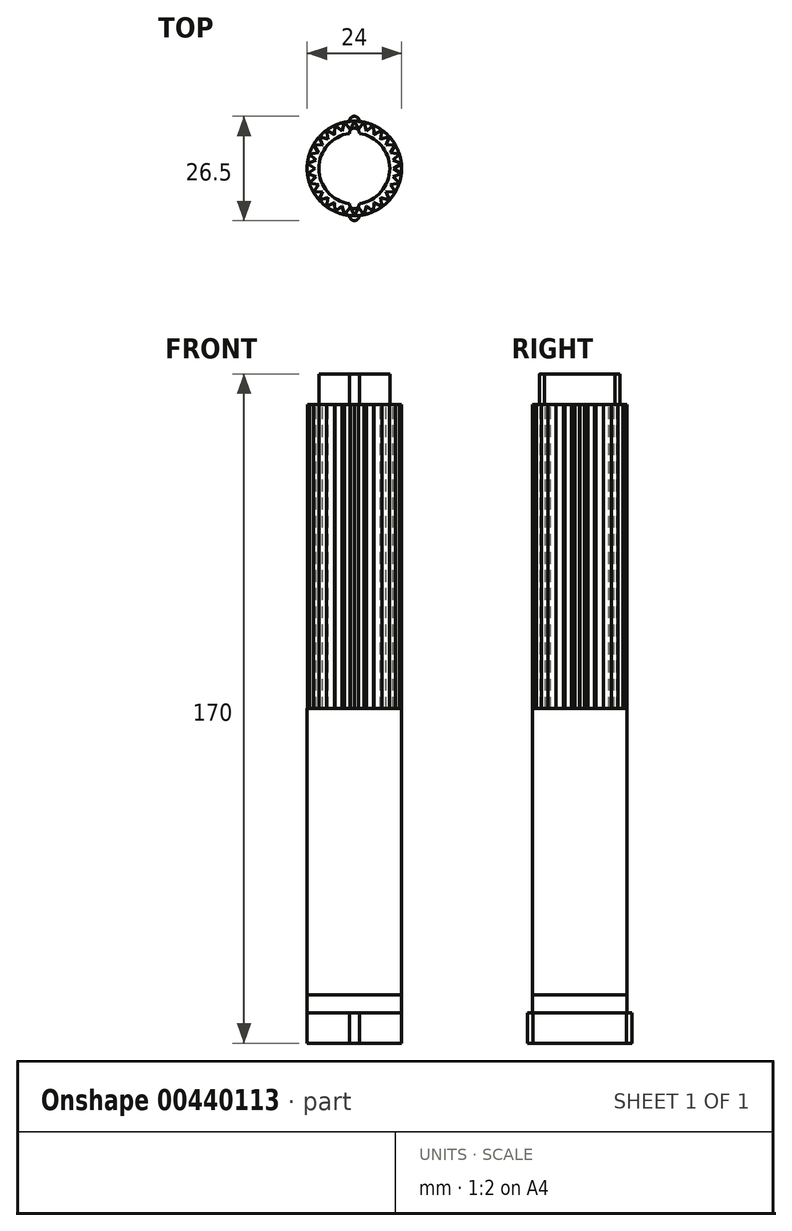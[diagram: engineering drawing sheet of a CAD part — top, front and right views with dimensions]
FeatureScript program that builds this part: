
annotation { "Feature Type Name" : "Feature", "Feature Type Description" : "" }
export const myFeature = defineFeature(function(context is Context, id is Id, definition is map)
    precondition{}
    {
        {
            var Q0;
            Q0=qCreatedBy(makeId("Top.planeOp"),FACE);
            var sketch = newSketch(context, id + "F0", { "sketchPlane" : qUnion([Q0])});
            skCircle(sketch, "E0", {"center": v(0, 0) * mm, "radius": 12 * mm});
            skSolve(sketch);
        }
        {
            var Q0;
            Q0 = qSketchRegion(id + "F0", true);
            extrude(context, id + "F1", {"entities" : qUnion([Q0]), "depth" : 72.75 * mm});
        }
        {
            var Q0;
            Q0=qCreatedBy(makeId("Top.planeOp"),FACE);
            cPlane(context, id + "F2", {"entities" : qUnion([Q0]), "cplaneType" : CPlaneType.OFFSET, "offset" : 75 * mm, "width" : 150 * mm, "height" : 150 * mm});
        }
        {
            var Q0;
            Q0=qCreatedBy(makeId("Top.planeOp"),FACE);
            cPlane(context, id + "F3", {"entities" : qUnion([Q0]), "cplaneType" : CPlaneType.OFFSET, "offset" : 150 * mm, "width" : 150 * mm, "height" : 150 * mm});
        }
        {
            var Q0;
            Q0=qCreatedBy(id+"F3.planeOp",FACE);
            var sketch = newSketch(context, id + "F4", { "sketchPlane" : qUnion([Q0])});
            skCircle(sketch, "E1", {"center": v(0, 0) * mm, "radius": 9 * mm});
            skCircle(sketch, "E2", {"center": v(0, 9) * mm, "radius": 1.25 * mm});
            skCircle(sketch, "E3", {"center": v(0, -9) * mm, "radius": 1.25 * mm});
            skSolve(sketch);
        }
        {
            var Q0;
            Q0 = qSketchRegion(id + "F4", true);
            extrude(context, id + "F5", {"entities" : qUnion([Q0]), "operationType" : NewBodyOperationType.ADD, "depth" : 7.75 * mm});
        }
        {
            var Q0;
            Q0=qCreatedBy(id+"F3.planeOp",FACE);
            var sketch = newSketch(context, id + "F6", { "sketchPlane" : qUnion([Q0])});
            skCircle(sketch, "E4", {"center": v(0, 0) * mm, "radius": 10 * mm});
            skLineSegment(sketch, "E5", {"start": v(0, 12) * mm, "end": v(-1.04, 9.95) * mm});
            skLineSegment(sketch, "E6", {"start": v(0, 12) * mm, "end": v(1.04, 9.95) * mm});
            skLineSegment(sketch, "E7.1.0", {"start": v(-2.5, 11.74) * mm, "end": v(-3.08, 9.51) * mm});
            skLineSegment(sketch, "E7.1.1", {"start": v(-2.5, 11.74) * mm, "end": v(-1.06, 9.94) * mm});
            skLineSegment(sketch, "E7.2.0", {"start": v(-4.88, 10.96) * mm, "end": v(-5, 8.67) * mm});
            skLineSegment(sketch, "E7.2.1", {"start": v(-4.88, 10.96) * mm, "end": v(-3.1, 9.5) * mm});
            skLineSegment(sketch, "E7.3.0", {"start": v(-7.05, 9.7) * mm, "end": v(-6.68, 7.44) * mm});
            skLineSegment(sketch, "E7.3.1", {"start": v(-7.05, 9.7) * mm, "end": v(-5, 8.66) * mm});
            skLineSegment(sketch, "E7.4.0", {"start": v(-8.92, 8.03) * mm, "end": v(-8.08, 5.89) * mm});
            skLineSegment(sketch, "E7.4.1", {"start": v(-8.92, 8.03) * mm, "end": v(-6.7, 7.42) * mm});
            skLineSegment(sketch, "E7.5.0", {"start": v(-10.4, 6) * mm, "end": v(-9.13, 4.08) * mm});
            skLineSegment(sketch, "E7.5.1", {"start": v(-10.4, 6) * mm, "end": v(-8.1, 5.87) * mm});
            skLineSegment(sketch, "E7.6.0", {"start": v(-11.41, 3.7) * mm, "end": v(-9.78, 2.09) * mm});
            skLineSegment(sketch, "E7.6.1", {"start": v(-11.41, 3.7) * mm, "end": v(-9.14, 4.06) * mm});
            skLineSegment(sketch, "E7.7.0", {"start": v(-11.93, 1.25) * mm, "end": v(-10, 0) * mm});
            skLineSegment(sketch, "E7.7.1", {"start": v(-11.93, 1.25) * mm, "end": v(-9.78, 2.07) * mm});
            skLineSegment(sketch, "E7.8.0", {"start": v(-11.93, -1.25) * mm, "end": v(-9.78, -2.07) * mm});
            skLineSegment(sketch, "E7.8.1", {"start": v(-11.93, -1.25) * mm, "end": v(-10, 0) * mm});
            skLineSegment(sketch, "E7.9.0", {"start": v(-11.41, -3.7) * mm, "end": v(-9.14, -4.06) * mm});
            skLineSegment(sketch, "E7.9.1", {"start": v(-11.41, -3.7) * mm, "end": v(-9.78, -2.09) * mm});
            skLineSegment(sketch, "E7.10.0", {"start": v(-10.4, -6) * mm, "end": v(-8.1, -5.87) * mm});
            skLineSegment(sketch, "E7.10.1", {"start": v(-10.4, -6) * mm, "end": v(-9.13, -4.08) * mm});
            skLineSegment(sketch, "E7.11.0", {"start": v(-8.92, -8.03) * mm, "end": v(-6.7, -7.42) * mm});
            skLineSegment(sketch, "E7.11.1", {"start": v(-8.92, -8.03) * mm, "end": v(-8.08, -5.89) * mm});
            skLineSegment(sketch, "E7.12.0", {"start": v(-7.05, -9.7) * mm, "end": v(-5, -8.66) * mm});
            skLineSegment(sketch, "E7.12.1", {"start": v(-7.05, -9.7) * mm, "end": v(-6.68, -7.44) * mm});
            skLineSegment(sketch, "E7.13.0", {"start": v(-4.88, -10.96) * mm, "end": v(-3.1, -9.5) * mm});
            skLineSegment(sketch, "E7.13.1", {"start": v(-4.88, -10.96) * mm, "end": v(-5, -8.67) * mm});
            skLineSegment(sketch, "E7.14.0", {"start": v(-2.5, -11.74) * mm, "end": v(-1.06, -9.94) * mm});
            skLineSegment(sketch, "E7.14.1", {"start": v(-2.5, -11.74) * mm, "end": v(-3.08, -9.51) * mm});
            skLineSegment(sketch, "E7.15.0", {"start": v(0, -12) * mm, "end": v(1.04, -9.95) * mm});
            skLineSegment(sketch, "E7.15.1", {"start": v(0, -12) * mm, "end": v(-1.04, -9.95) * mm});
            skLineSegment(sketch, "E7.16.0", {"start": v(2.5, -11.74) * mm, "end": v(3.08, -9.51) * mm});
            skLineSegment(sketch, "E7.16.1", {"start": v(2.5, -11.74) * mm, "end": v(1.06, -9.94) * mm});
            skLineSegment(sketch, "E7.17.0", {"start": v(4.88, -10.96) * mm, "end": v(5, -8.67) * mm});
            skLineSegment(sketch, "E7.17.1", {"start": v(4.88, -10.96) * mm, "end": v(3.1, -9.5) * mm});
            skLineSegment(sketch, "E7.18.0", {"start": v(7.05, -9.7) * mm, "end": v(6.68, -7.44) * mm});
            skLineSegment(sketch, "E7.18.1", {"start": v(7.05, -9.7) * mm, "end": v(5, -8.66) * mm});
            skLineSegment(sketch, "E7.19.0", {"start": v(8.92, -8.03) * mm, "end": v(8.08, -5.89) * mm});
            skLineSegment(sketch, "E7.19.1", {"start": v(8.92, -8.03) * mm, "end": v(6.7, -7.42) * mm});
            skLineSegment(sketch, "E7.20.0", {"start": v(10.4, -6) * mm, "end": v(9.13, -4.08) * mm});
            skLineSegment(sketch, "E7.20.1", {"start": v(10.4, -6) * mm, "end": v(8.1, -5.87) * mm});
            skLineSegment(sketch, "E7.21.0", {"start": v(11.41, -3.7) * mm, "end": v(9.78, -2.09) * mm});
            skLineSegment(sketch, "E7.21.1", {"start": v(11.41, -3.7) * mm, "end": v(9.14, -4.06) * mm});
            skLineSegment(sketch, "E7.22.0", {"start": v(11.93, -1.25) * mm, "end": v(10, 0) * mm});
            skLineSegment(sketch, "E7.22.1", {"start": v(11.93, -1.25) * mm, "end": v(9.78, -2.07) * mm});
            skLineSegment(sketch, "E7.23.0", {"start": v(11.93, 1.25) * mm, "end": v(9.78, 2.07) * mm});
            skLineSegment(sketch, "E7.23.1", {"start": v(11.93, 1.25) * mm, "end": v(10, 0) * mm});
            skLineSegment(sketch, "E7.24.0", {"start": v(11.41, 3.7) * mm, "end": v(9.14, 4.06) * mm});
            skLineSegment(sketch, "E7.24.1", {"start": v(11.41, 3.7) * mm, "end": v(9.78, 2.09) * mm});
            skLineSegment(sketch, "E7.25.0", {"start": v(10.4, 6) * mm, "end": v(8.1, 5.87) * mm});
            skLineSegment(sketch, "E7.25.1", {"start": v(10.4, 6) * mm, "end": v(9.13, 4.08) * mm});
            skLineSegment(sketch, "E7.26.0", {"start": v(8.92, 8.03) * mm, "end": v(6.7, 7.42) * mm});
            skLineSegment(sketch, "E7.26.1", {"start": v(8.92, 8.03) * mm, "end": v(8.08, 5.89) * mm});
            skLineSegment(sketch, "E7.27.0", {"start": v(7.05, 9.7) * mm, "end": v(5, 8.66) * mm});
            skLineSegment(sketch, "E7.27.1", {"start": v(7.05, 9.7) * mm, "end": v(6.68, 7.44) * mm});
            skLineSegment(sketch, "E7.28.0", {"start": v(4.88, 10.96) * mm, "end": v(3.1, 9.5) * mm});
            skLineSegment(sketch, "E7.28.1", {"start": v(4.88, 10.96) * mm, "end": v(5, 8.67) * mm});
            skLineSegment(sketch, "E7.29.0", {"start": v(2.5, 11.74) * mm, "end": v(1.06, 9.94) * mm});
            skLineSegment(sketch, "E7.29.1", {"start": v(2.5, 11.74) * mm, "end": v(3.08, 9.51) * mm});
            skSolve(sketch);
        }
        {
            var Q0;
            Q0 = qSketchRegion(id + "F6", true);
            extrude(context, id + "F7", {"entities" : qUnion([Q0]), "operationType" : NewBodyOperationType.ADD, "oppositeDirection" : true, "depth" : 77.25 * mm});
        }
        {
            var Q0;
            Q0=qCreatedBy(makeId("Top.planeOp"),FACE);
            cPlane(context, id + "F8", {"entities" : qUnion([Q0]), "cplaneType" : CPlaneType.OFFSET, "offset" : 4.5 * mm, "oppositeDirection" : true, "width" : 150 * mm, "height" : 150 * mm});
        }
        {
            var Q0;
            Q0=qCreatedBy(id+"F8.planeOp",FACE);
            var sketch = newSketch(context, id + "F9", { "sketchPlane" : qUnion([Q0])});
            skCircle(sketch, "E8", {"center": v(0, 0) * mm, "radius": 12 * mm});
            skCircle(sketch, "E9", {"center": v(0, -12) * mm, "radius": 1.25 * mm});
            skCircle(sketch, "E10", {"center": v(0, 12) * mm, "radius": 1.25 * mm});
            skSolve(sketch);
        }
        {
            var Q0;
            Q0 = qSketchRegion(id + "F9", true);
            extrude(context, id + "F10", {"entities" : qUnion([Q0]), "oppositeDirection" : true, "depth" : 7.75 * mm});
        }
        {
            var Q0;
            Q0=qCreatedBy(id+"F8.planeOp",FACE);
            var sketch = newSketch(context, id + "F11", { "sketchPlane" : qUnion([Q0])});
            skCircle(sketch, "E11", {"center": v(0, 0) * mm, "radius": 12 * mm});
            skSolve(sketch);
        }
        {
            var Q0;
            Q0 = qSketchRegion(id + "F11", true);
            extrude(context, id + "F12", {"entities" : qUnion([Q0]), "depth" : 4.5 * mm});
        }
    });
